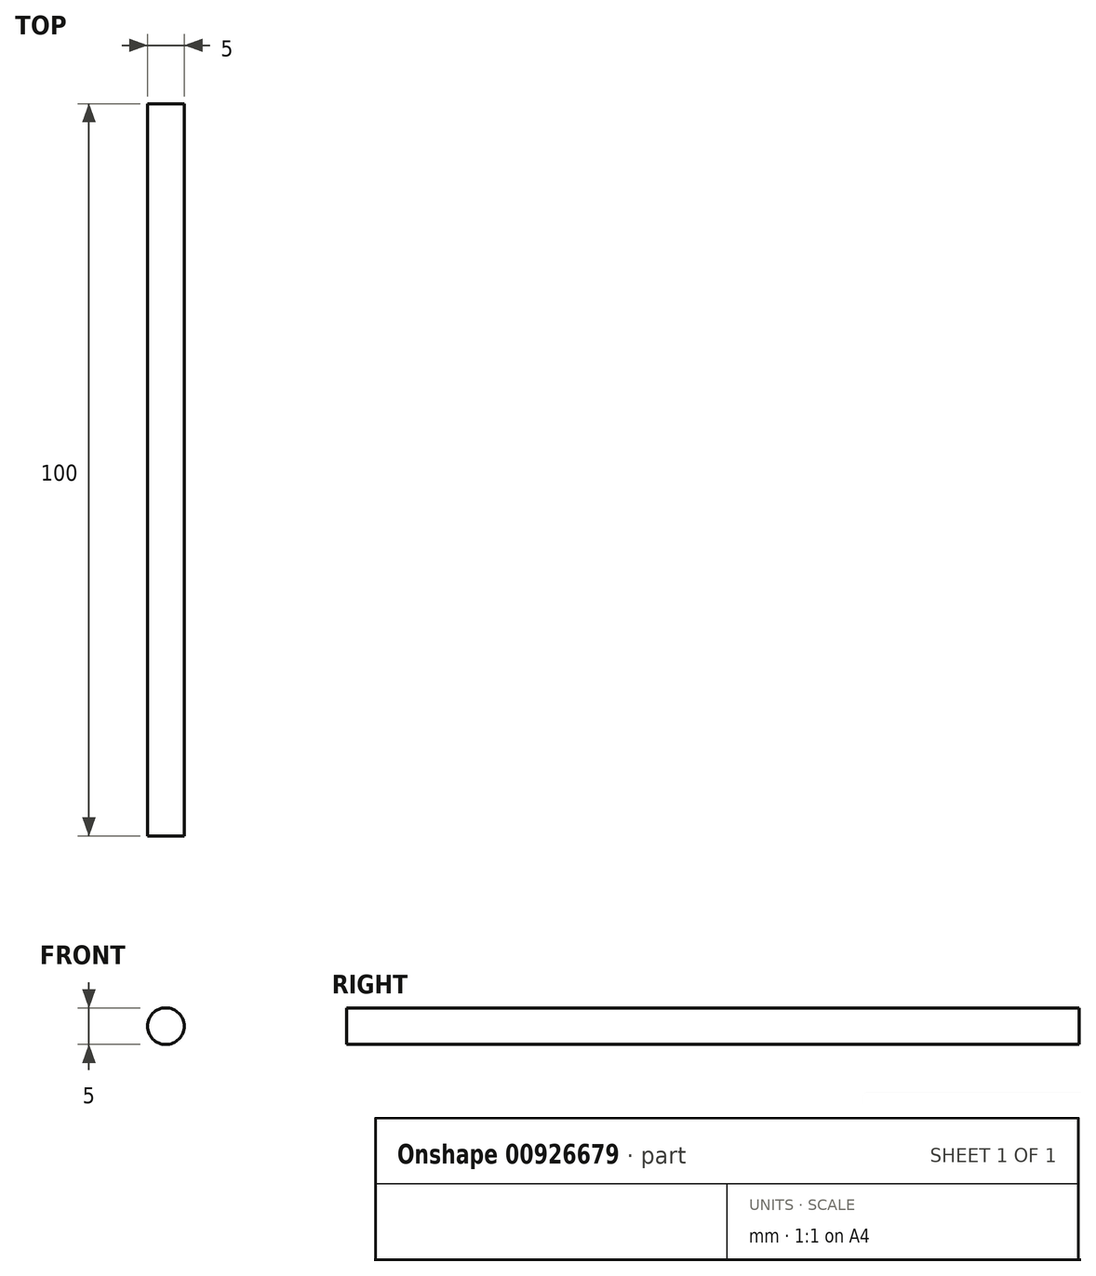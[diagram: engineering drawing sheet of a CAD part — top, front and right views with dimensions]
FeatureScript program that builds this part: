
annotation { "Feature Type Name" : "Feature", "Feature Type Description" : "" }
export const myFeature = defineFeature(function(context is Context, id is Id, definition is map)
    precondition{}
    {
        {
            var Q0;
            Q0=qCreatedBy(makeId("Front.planeOp"),FACE);
            var sketch = newSketch(context, id + "F0", { "sketchPlane" : qUnion([Q0])});
            skCircle(sketch, "E0", {"center": v(0, 0) * mm, "radius": 2.5 * mm});
            skSolve(sketch);
        }
        {
            var Q0;
            Q0 = qSketchRegion(id + "F0", true);
            extrude(context, id + "F1", {"entities" : qUnion([Q0]), "depth" : 100 * mm, "offsetDistance" : 25 * mm});
        }
    });
